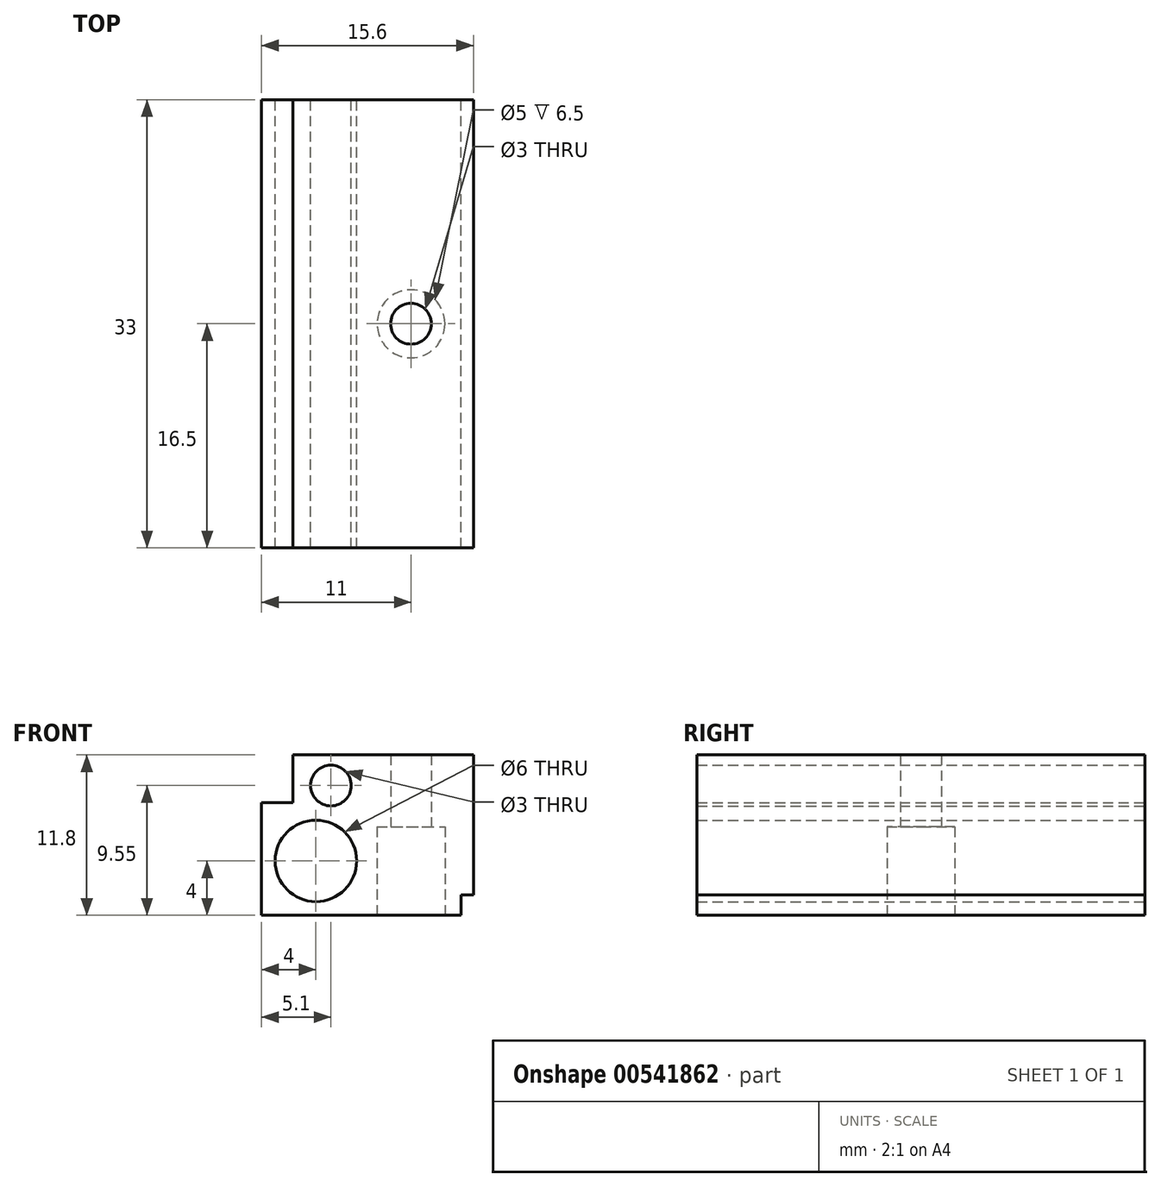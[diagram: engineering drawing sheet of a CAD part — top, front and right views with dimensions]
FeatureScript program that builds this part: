
annotation { "Feature Type Name" : "Feature", "Feature Type Description" : "" }
export const myFeature = defineFeature(function(context is Context, id is Id, definition is map)
    precondition{}
    {
        {
            var Q0;
            Q0=qCreatedBy(makeId("Front.planeOp"),FACE);
            var sketch = newSketch(context, id + "F0", { "sketchPlane" : qUnion([Q0])});
            skLineSegment(sketch, "E0", {"start": v(0, 0) * mm, "end": v(0, 8.3) * mm});
            skLineSegment(sketch, "E1", {"start": v(0, 8.3) * mm, "end": v(2.3, 8.3) * mm});
            skLineSegment(sketch, "E2", {"start": v(2.3, 8.3) * mm, "end": v(2.3, 11.8) * mm});
            skLineSegment(sketch, "E3", {"start": v(2.3, 11.8) * mm, "end": v(15.6, 11.8) * mm});
            skLineSegment(sketch, "E4", {"start": v(15.6, 11.8) * mm, "end": v(15.6, 1.5) * mm});
            skLineSegment(sketch, "E5", {"start": v(15.6, 1.5) * mm, "end": v(14.7, 1.5) * mm});
            skLineSegment(sketch, "E6", {"start": v(14.7, 1.5) * mm, "end": v(14.7, 0) * mm});
            skLineSegment(sketch, "E7", {"start": v(14.7, 0) * mm, "end": v(0, 0) * mm});
            skCircle(sketch, "E8", {"center": v(4, 4) * mm, "radius": 3 * mm});
            skCircle(sketch, "E9", {"center": v(5.1, 9.55) * mm, "radius": 1.5 * mm});
            skSolve(sketch);
        }
        {
            var Q0;
            Q0=makeQuery(id+"F0.imprint","IMPRINT",FACE,{"disambiguationData":[TD([[makeQuery(id+"F0.imprint","IMPRINT",EDGE,{"derivedFrom":sQuery(id+"F0.wireOp",EDGE,"E0")}),-1.0]])]});
            extrude(context, id + "F1", {"entities" : qUnion([Q0]), "depth" : 16.5 * mm, "offsetDistance" : 25 * mm, "hasSecondDirection" : true, "secondDirectionOppositeDirection" : true, "secondDirectionDepth" : 16.5 * mm});
        }
        {
            var Q0;
            Q0=makeQuery(id+"F1.opExtrude","SWEPT_FACE",FACE,{"disambiguationData":[OSD([sQuery(id+"F0.wireOp",EDGE,"E7")])]});
            var sketch = newSketch(context, id + "F2", { "sketchPlane" : qUnion([Q0])});
            skCircle(sketch, "E10", {"center": v(11, 0) * mm, "radius": 2.5 * mm});
            skCircle(sketch, "E11", {"center": v(11, 0) * mm, "radius": 1.5 * mm});
            skSolve(sketch);
        }
        {
            var Q0;
            Q0=makeQuery(id+"F2.imprint","IMPRINT",FACE,{"disambiguationData":[TD([[makeQuery(id+"F2.imprint","IMPRINT",EDGE,{"derivedFrom":sQuery(id+"F2.wireOp",EDGE,"E11")}),1.0]])]});
            var Q1;
            Q1=makeQuery(id+"F2.imprint","IMPRINT",FACE,{"disambiguationData":[TD([[makeQuery(id+"F2.imprint","IMPRINT",EDGE,{"derivedFrom":sQuery(id+"F2.wireOp",EDGE,"E10")}),1.0]])]});
            extrude(context, id + "F3", {"entities" : qUnion([Q0, Q1]), "operationType" : NewBodyOperationType.REMOVE, "oppositeDirection" : true, "depth" : 6.5 * mm, "offsetDistance" : 25 * mm});
        }
        {
            var Q0;
            Q0=makeQuery(id+"F2.imprint","IMPRINT",FACE,{"disambiguationData":[TD([[makeQuery(id+"F2.imprint","IMPRINT",EDGE,{"derivedFrom":sQuery(id+"F2.wireOp",EDGE,"E11")}),1.0]])]});
            var Q1;
            Q1=makeQuery(id+"F1.opExtrude","SWEPT_FACE",FACE,{"disambiguationData":[OSD([sQuery(id+"F0.wireOp",EDGE,"E3")])]});
            extrude(context, id + "F4", {"entities" : qUnion([Q0]), "operationType" : NewBodyOperationType.REMOVE, "endBound" : BoundingType.UP_TO_SURFACE, "oppositeDirection" : true, "depth" : 25 * mm, "endBoundEntityFace" : qUnion([Q1]), "offsetDistance" : 25 * mm});
        }
    });
